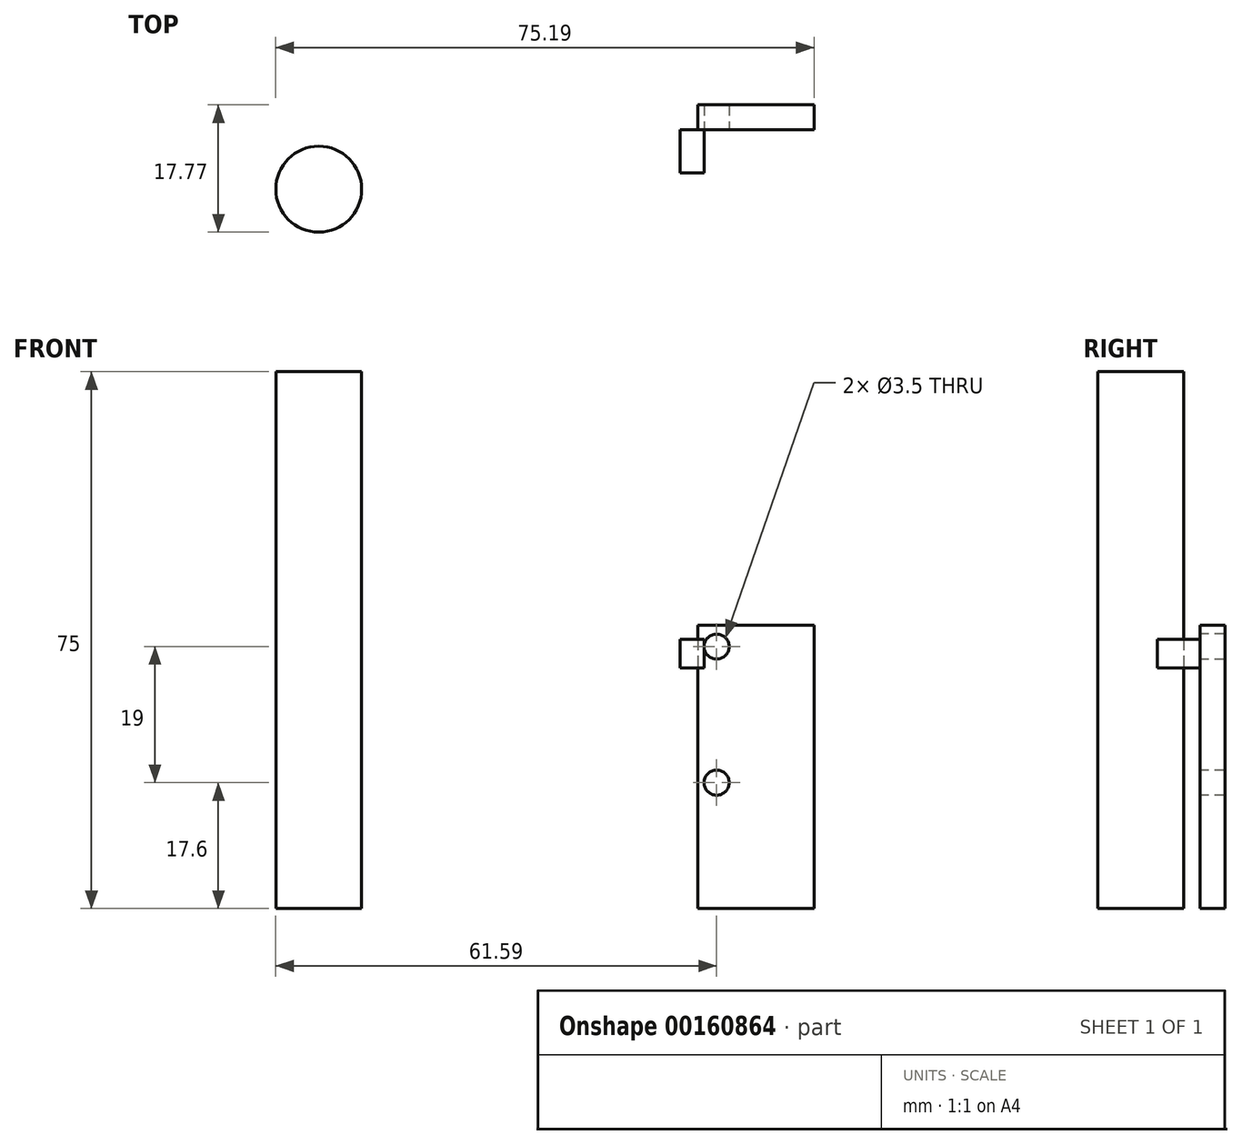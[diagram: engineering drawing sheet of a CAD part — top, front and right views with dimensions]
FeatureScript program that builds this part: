
annotation { "Feature Type Name" : "Feature", "Feature Type Description" : "" }
export const myFeature = defineFeature(function(context is Context, id is Id, definition is map)
    precondition{}
    {
        {
            var Q0;
            Q0=qCreatedBy(makeId("Top.planeOp"),FACE);
            var sketch = newSketch(context, id + "F0", { "sketchPlane" : qUnion([Q0])});
            skCircle(sketch, "E0", {"center": v(-69.19, -8.27) * mm, "radius": 6 * mm});
            skSolve(sketch);
        }
        {
            var Q0;
            Q0 = qSketchRegion(id + "F0", true);
            extrude(context, id + "F1", {"entities" : qUnion([Q0]), "depth" : 75 * mm});
        }
        {
            var Q0;
            Q0=qCreatedBy(makeId("Front.planeOp"),FACE);
            var sketch = newSketch(context, id + "F2", { "sketchPlane" : qUnion([Q0])});
            skLineSegment(sketch, "E1.bottom", {"start": v(-16.2, 39.6) * mm, "end": v(0, 39.6) * mm});
            skLineSegment(sketch, "E1.top", {"start": v(-16.2, 0) * mm, "end": v(0, 0) * mm});
            skLineSegment(sketch, "E1.left", {"start": v(-16.2, 39.6) * mm, "end": v(-16.2, 0) * mm});
            skLineSegment(sketch, "E1.right", {"start": v(0, 39.6) * mm, "end": v(0, 0) * mm});
            skCircle(sketch, "E2", {"center": v(-13.6, 36.6) * mm, "radius": 1.75 * mm});
            skCircle(sketch, "E3", {"center": v(-13.6, 17.6) * mm, "radius": 1.75 * mm});
            skSolve(sketch);
        }
        {
            var Q0;
            Q0 = qSketchRegion(id + "F2", true);
            extrude(context, id + "F3", {"entities" : qUnion([Q0]), "oppositeDirection" : true, "depth" : 3.5 * mm});
        }
        {
            var Q0;
            Q0=qCreatedBy(makeId("Front.planeOp"),FACE);
            var sketch = newSketch(context, id + "F4", { "sketchPlane" : qUnion([Q0])});
            skLineSegment(sketch, "E4.bottom", {"start": v(-18.7, 37.6) * mm, "end": v(-15.35, 37.6) * mm});
            skLineSegment(sketch, "E4.top", {"start": v(-18.7, 33.6) * mm, "end": v(-15.35, 33.6) * mm});
            skLineSegment(sketch, "E4.left", {"start": v(-18.7, 37.6) * mm, "end": v(-18.7, 33.6) * mm});
            skLineSegment(sketch, "E4.right", {"start": v(-15.35, 37.6) * mm, "end": v(-15.35, 33.6) * mm});
            skPoint(sketch, "E5", {"position": v(-18.7, 35.6) * mm});
            skPoint(sketch, "E6", {"position": v(-13.6, 36.6) * mm});
            skPoint(sketch, "E7", {"position": v(-15.35, 36.6) * mm});
            skSolve(sketch);
        }
        {
            var Q0;
            Q0 = qSketchRegion(id + "F4", true);
            extrude(context, id + "F5", {"entities" : qUnion([Q0]), "operationType" : NewBodyOperationType.ADD, "depth" : 6 * mm});
        }
    });
